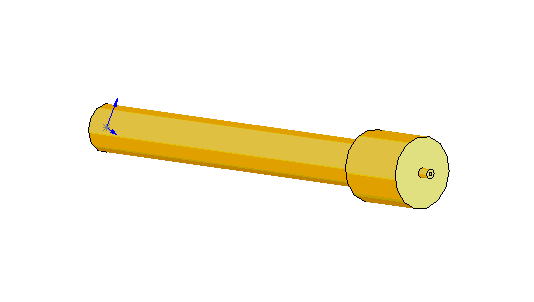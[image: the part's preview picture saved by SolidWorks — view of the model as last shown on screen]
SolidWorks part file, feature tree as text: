
SOLIDWORKS PART (.sldprt)
format: sldprt  version: not decoded by parser v0  size: 103,936 bytes
history: native  units: mm
features: sketch x3, extrude x3 (+11 scaffold rows collapsed)
feature tree (17):
  scaffold x11  (default folders/planes/origin — collapsed)
  sketch  "Sketch1"  dims[D1=6.35mm D2=3.302mm]
  extrude  "Extrude1"  Depth=50.8mm
  sketch  "Sketch2"  dims[D1=9.525mm]
  extrude  "Extrude2"  Depth=9.525mm
  sketch  "Sketch3"  dims[D1=~1.29667mm D2=0.508mm]
  extrude  "Extrude3"  Depth=1.5875mm
decode coverage: 6 of 6 modeling features carry decoded parameters
note: ~ marks probable driven/reference dimensions
note: suppression state not decoded; provenance and decode notes live in map.json
